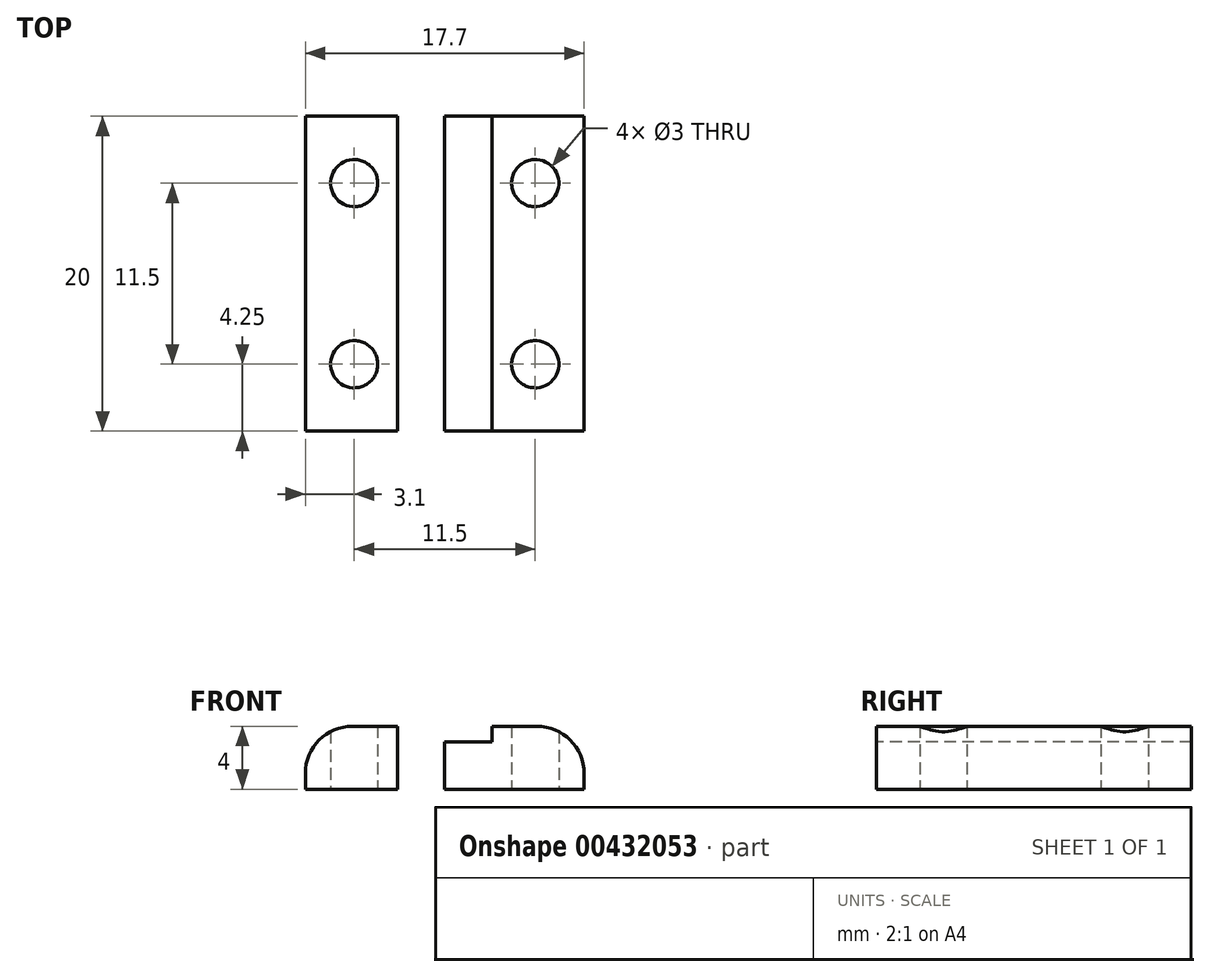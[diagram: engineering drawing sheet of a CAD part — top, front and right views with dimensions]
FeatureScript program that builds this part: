
annotation { "Feature Type Name" : "Feature", "Feature Type Description" : "" }
export const myFeature = defineFeature(function(context is Context, id is Id, definition is map)
    precondition{}
    {
        {
            var Q0;
            Q0=qCreatedBy(makeId("Top.planeOp"),FACE);
            var sketch = newSketch(context, id + "F0", { "sketchPlane" : qUnion([Q0])});
            skLineSegment(sketch, "E0.bottom", {"start": v(8.85, -10) * mm, "end": v(-8.85, -10) * mm});
            skLineSegment(sketch, "E0.top", {"start": v(8.85, 10) * mm, "end": v(-8.85, 10) * mm});
            skLineSegment(sketch, "E0.left", {"start": v(8.85, -10) * mm, "end": v(8.85, 10) * mm});
            skLineSegment(sketch, "E0.right", {"start": v(-8.85, -10) * mm, "end": v(-8.85, 10) * mm});
            skPoint(sketch, "E0.middle", {"position": v(0, 0) * mm});
            skCircle(sketch, "E1", {"center": v(-5.75, 5.75) * mm, "radius": 1.5 * mm});
            skCircle(sketch, "E2.0.1.0", {"center": v(-5.75, -5.75) * mm, "radius": 1.5 * mm});
            skCircle(sketch, "E2.1.0.0", {"center": v(5.75, 5.75) * mm, "radius": 1.5 * mm});
            skCircle(sketch, "E2.1.1.0", {"center": v(5.75, -5.75) * mm, "radius": 1.5 * mm});
            skLineSegment(sketch, "E2.direction1", {"start": v(-5.75, 5.75) * mm, "end": v(5.75, 5.75) * mm, "construction": true});
            skLineSegment(sketch, "E2.direction2", {"start": v(-5.75, 5.75) * mm, "end": v(-5.75, -5.75) * mm, "construction": true});
            skLineSegment(sketch, "E3.bottom", {"start": v(0, 10) * mm, "end": v(-3, 10) * mm});
            skLineSegment(sketch, "E3.top", {"start": v(0, -10) * mm, "end": v(-3, -10) * mm});
            skLineSegment(sketch, "E3.left", {"start": v(0, 10) * mm, "end": v(0, -10) * mm});
            skLineSegment(sketch, "E3.right", {"start": v(-3, 10) * mm, "end": v(-3, -10) * mm});
            skLineSegment(sketch, "E4.MirrorCS", {"start": v(3, 10) * mm, "end": v(3, -10) * mm});
            skLineSegment(sketch, "E5.MirrorCS", {"start": v(0, 10) * mm, "end": v(3, 10) * mm});
            skLineSegment(sketch, "E6.MirrorCS", {"start": v(0, -10) * mm, "end": v(3, -10) * mm});
            skCircle(sketch, "E7.cCircle", {"center": v(-5.75, -5.75) * mm, "radius": 2.75 * mm, "construction": true});
            skLineSegment(sketch, "E7.0", {"start": v(-3, -4.16) * mm, "end": v(-3, -7.34) * mm});
            skLineSegment(sketch, "E7.1", {"start": v(-3, -7.34) * mm, "end": v(-5.75, -8.93) * mm});
            skLineSegment(sketch, "E7.2", {"start": v(-5.75, -8.93) * mm, "end": v(-8.5, -7.34) * mm});
            skLineSegment(sketch, "E7.3", {"start": v(-8.5, -7.34) * mm, "end": v(-8.5, -4.16) * mm});
            skLineSegment(sketch, "E7.4", {"start": v(-8.5, -4.16) * mm, "end": v(-5.75, -2.57) * mm});
            skLineSegment(sketch, "E7.5", {"start": v(-5.75, -2.57) * mm, "end": v(-3, -4.16) * mm});
            skPoint(sketch, "E7.0.midPoint", {"position": v(-3, -5.75) * mm});
            skCircle(sketch, "E8.cCircle", {"center": v(5.75, -5.75) * mm, "radius": 2.75 * mm, "construction": true});
            skLineSegment(sketch, "E8.0", {"start": v(3, -7.34) * mm, "end": v(3, -4.16) * mm});
            skLineSegment(sketch, "E8.1", {"start": v(3, -4.16) * mm, "end": v(5.75, -2.57) * mm});
            skLineSegment(sketch, "E8.2", {"start": v(5.75, -2.57) * mm, "end": v(8.5, -4.16) * mm});
            skLineSegment(sketch, "E8.3", {"start": v(8.5, -4.16) * mm, "end": v(8.5, -7.34) * mm});
            skLineSegment(sketch, "E8.4", {"start": v(8.5, -7.34) * mm, "end": v(5.75, -8.93) * mm});
            skLineSegment(sketch, "E8.5", {"start": v(5.75, -8.93) * mm, "end": v(3, -7.34) * mm});
            skPoint(sketch, "E8.0.midPoint", {"position": v(3, -5.75) * mm});
            skCircle(sketch, "E9.cCircle", {"center": v(5.75, 5.75) * mm, "radius": 2.75 * mm, "construction": true});
            skLineSegment(sketch, "E9.0", {"start": v(3, 4.16) * mm, "end": v(3, 7.34) * mm});
            skLineSegment(sketch, "E9.1", {"start": v(3, 7.34) * mm, "end": v(5.75, 8.93) * mm});
            skLineSegment(sketch, "E9.2", {"start": v(5.75, 8.93) * mm, "end": v(8.5, 7.34) * mm});
            skLineSegment(sketch, "E9.3", {"start": v(8.5, 7.34) * mm, "end": v(8.5, 4.16) * mm});
            skLineSegment(sketch, "E9.4", {"start": v(8.5, 4.16) * mm, "end": v(5.75, 2.57) * mm});
            skLineSegment(sketch, "E9.5", {"start": v(5.75, 2.57) * mm, "end": v(3, 4.16) * mm});
            skPoint(sketch, "E9.0.midPoint", {"position": v(3, 5.75) * mm});
            skCircle(sketch, "E10.cCircle", {"center": v(-5.75, 5.75) * mm, "radius": 2.75 * mm, "construction": true});
            skLineSegment(sketch, "E10.0", {"start": v(-3, 7.34) * mm, "end": v(-3, 4.16) * mm});
            skLineSegment(sketch, "E10.1", {"start": v(-3, 4.16) * mm, "end": v(-5.75, 2.57) * mm});
            skLineSegment(sketch, "E10.2", {"start": v(-5.75, 2.57) * mm, "end": v(-8.5, 4.16) * mm});
            skLineSegment(sketch, "E10.3", {"start": v(-8.5, 4.16) * mm, "end": v(-8.5, 7.34) * mm});
            skLineSegment(sketch, "E10.4", {"start": v(-8.5, 7.34) * mm, "end": v(-5.75, 8.93) * mm});
            skLineSegment(sketch, "E10.5", {"start": v(-5.75, 8.93) * mm, "end": v(-3, 7.34) * mm});
            skPoint(sketch, "E10.0.midPoint", {"position": v(-3, 5.75) * mm});
            skSolve(sketch);
        }
        {
            var Q0;
            {var subQ1=sQuery(id+"F0.wireOp",EDGE,"E0.right");Q0=makeQuery(id+"F0.imprint","IMPRINT",FACE,{"disambiguationData":[TD([[makeQuery(id+"F0.imprint","IMPRINT",EDGE,{"derivedFrom":subQ1}),-1.0]])]});}
            var Q1;
            {var subQ0=sQuery(id+"F0.wireOp",EDGE,"E0.left");Q1=makeQuery(id+"F0.imprint","IMPRINT",FACE,{"disambiguationData":[TD([[makeQuery(id+"F0.imprint","IMPRINT",EDGE,{"derivedFrom":subQ0}),1.0]])]});}
            var Q2;
            Q2=makeQuery(id+"F0.imprint","IMPRINT",FACE,{"disambiguationData":[TD([[makeQuery(id+"F0.imprint","IMPRINT",EDGE,{"derivedFrom":sQuery(id+"F0.wireOp",EDGE,"E2.0.1.0")}),-1.0]])]});
            var Q3;
            Q3=makeQuery(id+"F0.imprint","IMPRINT",FACE,{"disambiguationData":[TD([[makeQuery(id+"F0.imprint","IMPRINT",EDGE,{"derivedFrom":sQuery(id+"F0.wireOp",EDGE,"E2.1.1.0")}),-1.0]])]});
            var Q4;
            Q4=makeQuery(id+"F0.imprint","IMPRINT",FACE,{"disambiguationData":[TD([[makeQuery(id+"F0.imprint","IMPRINT",EDGE,{"derivedFrom":sQuery(id+"F0.wireOp",EDGE,"E2.1.0.0")}),-1.0]])]});
            var Q5;
            Q5=makeQuery(id+"F0.imprint","IMPRINT",FACE,{"disambiguationData":[TD([[makeQuery(id+"F0.imprint","IMPRINT",EDGE,{"derivedFrom":sQuery(id+"F0.wireOp",EDGE,"E1")}),-1.0]])]});
            extrude(context, id + "F1", {"entities" : qUnion([Q0, Q1, Q2, Q3, Q4, Q5]), "depth" : 4 * mm});
        }
        {
            var Q0;
            Q0=makeQuery(id+"F0.imprint","IMPRINT",FACE,{"disambiguationData":[TD([[makeQuery(id+"F0.imprint","IMPRINT",EDGE,{"derivedFrom":sQuery(id+"F0.wireOp",EDGE,"E3.bottom")}),1.0]])]});
            var Q1;
            Q1=makeQuery(id+"F0.imprint","IMPRINT",FACE,{"disambiguationData":[TD([[makeQuery(id+"F0.imprint","IMPRINT",EDGE,{"derivedFrom":sQuery(id+"F0.wireOp",EDGE,"E3.left")}),1.0]])]});
            extrude(context, id + "F2", {"entities" : qUnion([Q0, Q1]), "operationType" : NewBodyOperationType.ADD, "depth" : 3 * mm});
        }
        {
            var Q0;
            Q0=makeQuery(id+"F1.opExtrude","CAP_EDGE",EDGE,{"disambiguationData":[OSD([sQuery(id+"F0.wireOp",EDGE,"E0.left")])],"isStart":false});
            var Q1;
            Q1=makeQuery(id+"F1.opExtrude","CAP_EDGE",EDGE,{"disambiguationData":[OSD([sQuery(id+"F0.wireOp",EDGE,"E0.right")])],"isStart":false});
            fillet(context, id + "F3", {"entities" : qUnion([Q0, Q1]), "radius" : 3 * mm, "tangentPropagation" : true, "allowEdgeOverflow" : false});
        }
    });
